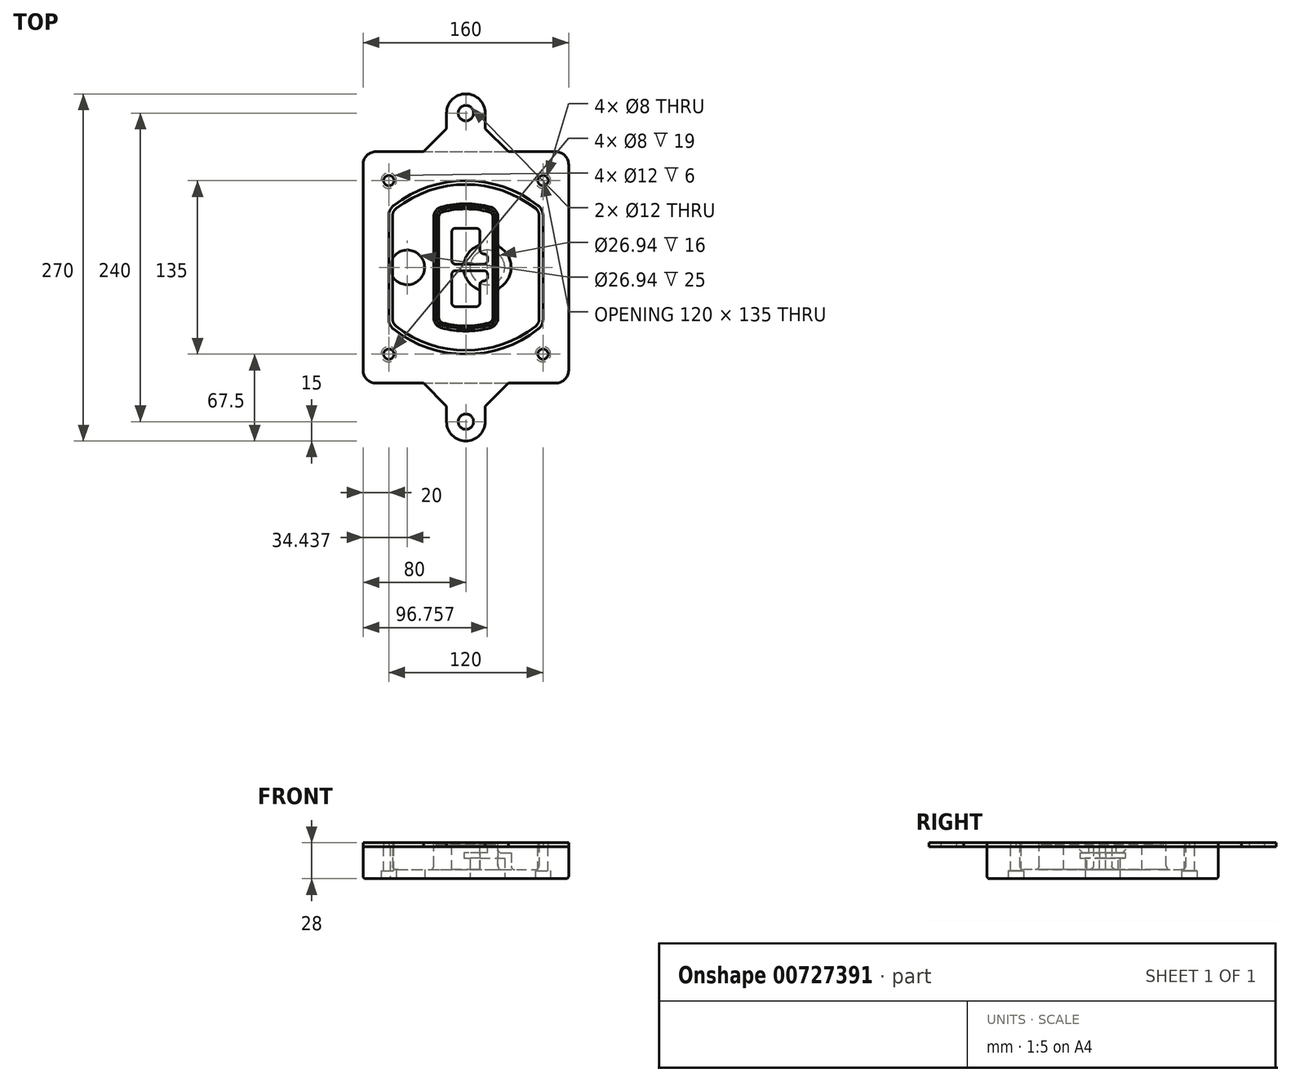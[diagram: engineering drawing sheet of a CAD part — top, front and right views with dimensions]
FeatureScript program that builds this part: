
annotation { "Feature Type Name" : "Feature", "Feature Type Description" : "" }
export const myFeature = defineFeature(function(context is Context, id is Id, definition is map)
    precondition{}
    {
        {
            var Q0;
            Q0=qCreatedBy(makeId("Top.planeOp"),FACE);
            var sketch = newSketch(context, id + "F0", { "sketchPlane" : qUnion([Q0])});
            skPoint(sketch, "E0.rect.middle", {"position": v(0, 0) * mm});
            skLineSegment(sketch, "E1.bottom", {"start": v(-70, -90) * mm, "end": v(70, -90) * mm});
            skLineSegment(sketch, "E1.top", {"start": v(-70, 90) * mm, "end": v(70, 90) * mm});
            skLineSegment(sketch, "E1.left", {"start": v(-80, -80) * mm, "end": v(-80, 80) * mm});
            skLineSegment(sketch, "E1.right", {"start": v(80, -80) * mm, "end": v(80, 80) * mm});
            skLineSegment(sketch, "E2", {"start": v(-80, 90) * mm, "end": v(80, -90) * mm, "construction": true});
            skLineSegment(sketch, "E3", {"start": v(80, 90) * mm, "end": v(-80, -90) * mm, "construction": true});
            skCircle(sketch, "E4", {"center": v(-60, 67.5) * mm, "radius": 4 * mm});
            skCircle(sketch, "E5", {"center": v(60, 67.5) * mm, "radius": 4 * mm});
            skCircle(sketch, "E6", {"center": v(60, -67.5) * mm, "radius": 4 * mm});
            skCircle(sketch, "E7", {"center": v(-60, -67.5) * mm, "radius": 4 * mm});
            skLineSegment(sketch, "E8", {"start": v(-60, 67.5) * mm, "end": v(60, 67.5) * mm, "construction": true});
            skLineSegment(sketch, "E9", {"start": v(60, 67.5) * mm, "end": v(60, -67.5) * mm, "construction": true});
            skLineSegment(sketch, "E10", {"start": v(60, -67.5) * mm, "end": v(-60, -67.5) * mm, "construction": true});
            skLineSegment(sketch, "E11", {"start": v(-60, -67.5) * mm, "end": v(-60, 67.5) * mm, "construction": true});
            skLineSegment(sketch, "E12", {"start": v(-60, 40.3) * mm, "end": v(-60, -40.3) * mm});
            skLineSegment(sketch, "E13", {"start": v(60, 40.3) * mm, "end": v(60, -40.3) * mm});
            skArc(sketch, "E14", {"start": v(56.15, 48.18) * mm, "mid": v(0, 67.5) * mm, "end": v(-56.15, 48.18) * mm});
            skArc(sketch, "E15", {"start": v(-56.15, -48.18) * mm, "mid": v(0, -67.5) * mm, "end": v(56.15, -48.18) * mm});
            skLineSegment(sketch, "E16", {"start": v(-60, 0) * mm, "end": v(60, 0) * mm, "construction": true});
            skPoint(sketch, "E17.visualSharp", {"position": v(-60, -45) * mm});
            skArc(sketch, "E17.filletArc", {"start": v(-60, -40.3) * mm, "mid": v(-58.99, -44.68) * mm, "end": v(-56.15, -48.18) * mm});
            skPoint(sketch, "E18.visualSharp", {"position": v(-60, 45) * mm});
            skArc(sketch, "E18.filletArc", {"start": v(-56.15, 48.18) * mm, "mid": v(-58.99, 44.68) * mm, "end": v(-60, 40.3) * mm});
            skPoint(sketch, "E19.visualSharp", {"position": v(60, 45) * mm});
            skArc(sketch, "E19.filletArc", {"start": v(60, 40.3) * mm, "mid": v(58.99, 44.68) * mm, "end": v(56.15, 48.18) * mm});
            skPoint(sketch, "E20.visualSharp", {"position": v(60, -45) * mm});
            skArc(sketch, "E20.filletArc", {"start": v(56.15, -48.18) * mm, "mid": v(58.99, -44.68) * mm, "end": v(60, -40.3) * mm});
            skPoint(sketch, "E21.visualSharp", {"position": v(-80, 90) * mm});
            skArc(sketch, "E21.filletArc", {"start": v(-70, 90) * mm, "mid": v(-77.07, 87.07) * mm, "end": v(-80, 80) * mm});
            skPoint(sketch, "E22.visualSharp", {"position": v(80, 90) * mm});
            skArc(sketch, "E22.filletArc", {"start": v(80, 80) * mm, "mid": v(77.07, 87.07) * mm, "end": v(70, 90) * mm});
            skPoint(sketch, "E23.visualSharp", {"position": v(80, -90) * mm});
            skArc(sketch, "E23.filletArc", {"start": v(70, -90) * mm, "mid": v(77.07, -87.07) * mm, "end": v(80, -80) * mm});
            skPoint(sketch, "E24.visualSharp", {"position": v(-80, -90) * mm});
            skArc(sketch, "E24.filletArc", {"start": v(-80, -80) * mm, "mid": v(-77.07, -87.07) * mm, "end": v(-70, -90) * mm});
            skArc(sketch, "E25.0", {"start": v(57, 40.3) * mm, "mid": v(56.3, 43.36) * mm, "end": v(54.3, 45.81) * mm});
            skLineSegment(sketch, "E25.1", {"start": v(57, 40.3) * mm, "end": v(57, -40.3) * mm});
            skArc(sketch, "E25.2", {"start": v(54.3, -45.81) * mm, "mid": v(56.3, -43.36) * mm, "end": v(57, -40.3) * mm});
            skArc(sketch, "E25.3", {"start": v(-54.3, -45.81) * mm, "mid": v(0, -64.5) * mm, "end": v(54.3, -45.81) * mm});
            skArc(sketch, "E25.4", {"start": v(-57, -40.3) * mm, "mid": v(-56.3, -43.36) * mm, "end": v(-54.3, -45.81) * mm});
            skArc(sketch, "E25.5", {"start": v(54.3, 45.81) * mm, "mid": v(0, 64.5) * mm, "end": v(-54.3, 45.81) * mm});
            skLineSegment(sketch, "E25.6", {"start": v(-57, 40.3) * mm, "end": v(-57, -40.3) * mm});
            skArc(sketch, "E25.7", {"start": v(-54.3, 45.81) * mm, "mid": v(-56.3, 43.36) * mm, "end": v(-57, 40.3) * mm});
            skArc(sketch, "E26.0", {"start": v(-58.62, 51.33) * mm, "mid": v(-62.58, 46.43) * mm, "end": v(-64, 40.3) * mm});
            skArc(sketch, "E26.1", {"start": v(58.62, 51.33) * mm, "mid": v(0, 71.5) * mm, "end": v(-58.62, 51.33) * mm});
            skArc(sketch, "E26.2", {"start": v(64, 40.3) * mm, "mid": v(62.58, 46.43) * mm, "end": v(58.62, 51.33) * mm});
            skLineSegment(sketch, "E26.3", {"start": v(64, 40.3) * mm, "end": v(64, -40.3) * mm});
            skArc(sketch, "E26.4", {"start": v(58.62, -51.33) * mm, "mid": v(62.58, -46.43) * mm, "end": v(64, -40.3) * mm});
            skLineSegment(sketch, "E26.5", {"start": v(-64, 40.3) * mm, "end": v(-64, -40.3) * mm});
            skArc(sketch, "E26.6", {"start": v(-58.62, -51.33) * mm, "mid": v(0, -71.5) * mm, "end": v(58.62, -51.33) * mm});
            skArc(sketch, "E26.7", {"start": v(-64, -40.3) * mm, "mid": v(-62.58, -46.43) * mm, "end": v(-58.62, -51.33) * mm});
            skSolve(sketch);
        }
        {
            var Q0;
            Q0=makeQuery(id+"F0.imprint","IMPRINT",FACE,{"disambiguationData":[TD([[makeQuery(id+"F0.imprint","IMPRINT",EDGE,{"derivedFrom":sQuery(id+"F0.wireOp",EDGE,"E1.bottom")}),1.0]])]});
            var Q1;
            Q1=makeQuery(id+"F0.imprint","IMPRINT",FACE,{"disambiguationData":[TD([[makeQuery(id+"F0.imprint","IMPRINT",EDGE,{"derivedFrom":sQuery(id+"F0.wireOp",EDGE,"E12")}),1.0]])]});
            var Q2;
            Q2=makeQuery(id+"F0.imprint","IMPRINT",FACE,{"disambiguationData":[TD([[makeQuery(id+"F0.imprint","IMPRINT",EDGE,{"derivedFrom":sQuery(id+"F0.wireOp",EDGE,"E25.0")}),1.0]])]});
            var Q3;
            Q3=makeQuery(id+"F0.imprint","IMPRINT",FACE,{"disambiguationData":[TD([[makeQuery(id+"F0.imprint","IMPRINT",EDGE,{"derivedFrom":sQuery(id+"F0.wireOp",EDGE,"E12")}),-1.0]])]});
            extrude(context, id + "F1", {"entities" : qUnion([Q0, Q1, Q2, Q3]), "oppositeDirection" : true, "depth" : 25 * mm});
        }
        {
            var Q0;
            Q0=makeQuery(id+"F0.imprint","IMPRINT",FACE,{"disambiguationData":[TD([[makeQuery(id+"F0.imprint","IMPRINT",EDGE,{"derivedFrom":sQuery(id+"F0.wireOp",EDGE,"E12")}),1.0]])]});
            extrude(context, id + "F2", {"entities" : qUnion([Q0]), "operationType" : NewBodyOperationType.ADD, "depth" : 3 * mm});
        }
        {
            var Q0;
            Q0=makeQuery(id+"F0.imprint","IMPRINT",FACE,{"disambiguationData":[TD([[makeQuery(id+"F0.imprint","IMPRINT",EDGE,{"derivedFrom":sQuery(id+"F0.wireOp",EDGE,"E25.0")}),1.0]])]});
            extrude(context, id + "F3", {"entities" : qUnion([Q0]), "operationType" : NewBodyOperationType.REMOVE, "oppositeDirection" : true, "depth" : 18 * mm});
        }
        {
            var Q0;
            Q0=makeQuery(id+"F2.opExtrude","CAP_FACE",FACE,{"disambiguationData":[OSD([sQuery(id+"F0.wireOp",EDGE,"E12"),sQuery(id+"F0.wireOp",EDGE,"E13"),sQuery(id+"F0.wireOp",EDGE,"E14"),sQuery(id+"F0.wireOp",EDGE,"E15"),sQuery(id+"F0.wireOp",EDGE,"E17.filletArc"),sQuery(id+"F0.wireOp",EDGE,"E18.filletArc"),sQuery(id+"F0.wireOp",EDGE,"E19.filletArc"),sQuery(id+"F0.wireOp",EDGE,"E20.filletArc"),sQuery(id+"F0.wireOp",EDGE,"E25.0"),sQuery(id+"F0.wireOp",EDGE,"E25.1"),sQuery(id+"F0.wireOp",EDGE,"E25.2"),sQuery(id+"F0.wireOp",EDGE,"E25.3"),sQuery(id+"F0.wireOp",EDGE,"E25.4"),sQuery(id+"F0.wireOp",EDGE,"E25.5"),sQuery(id+"F0.wireOp",EDGE,"E25.6"),sQuery(id+"F0.wireOp",EDGE,"E25.7")])],"isStart":false});
            var sketch = newSketch(context, id + "F4", { "sketchPlane" : qUnion([Q0])});
            skArc(sketch, "E27.0", {"start": v(-19.08, -46.97) * mm, "mid": v(0, -49.5) * mm, "end": v(19.08, -46.97) * mm});
            skArc(sketch, "E28.0", {"start": v(19.08, 46.97) * mm, "mid": v(0, 49.5) * mm, "end": v(-19.08, 46.97) * mm});
            skLineSegment(sketch, "E29", {"start": v(-25, 39.25) * mm, "end": v(-25, -39.25) * mm});
            skLineSegment(sketch, "E30", {"start": v(25, 39.25) * mm, "end": v(25, -39.25) * mm});
            skLineSegment(sketch, "E31", {"start": v(-25, 45.1) * mm, "end": v(25, 45.1) * mm, "construction": true});
            skLineSegment(sketch, "E32", {"start": v(-25, -45.1) * mm, "end": v(25, -45.1) * mm, "construction": true});
            skPoint(sketch, "E33.visualSharp", {"position": v(-25, 45.1) * mm});
            skArc(sketch, "E33.filletArc", {"start": v(-19.08, 46.97) * mm, "mid": v(-23.35, 44.11) * mm, "end": v(-25, 39.25) * mm});
            skPoint(sketch, "E34.visualSharp", {"position": v(25, 45.1) * mm});
            skArc(sketch, "E34.filletArc", {"start": v(25, 39.25) * mm, "mid": v(23.35, 44.11) * mm, "end": v(19.08, 46.97) * mm});
            skPoint(sketch, "E35.visualSharp", {"position": v(25, -45.1) * mm});
            skArc(sketch, "E35.filletArc", {"start": v(19.08, -46.97) * mm, "mid": v(23.35, -44.11) * mm, "end": v(25, -39.25) * mm});
            skPoint(sketch, "E36.visualSharp", {"position": v(-25, -45.1) * mm});
            skArc(sketch, "E36.filletArc", {"start": v(-25, -39.25) * mm, "mid": v(-23.35, -44.11) * mm, "end": v(-19.08, -46.97) * mm});
            skArc(sketch, "E37.0", {"start": v(54.3, 45.81) * mm, "mid": v(0, 64.5) * mm, "end": v(-54.3, 45.81) * mm});
            skArc(sketch, "E37.1", {"start": v(-54.3, 45.81) * mm, "mid": v(-56.3, 43.36) * mm, "end": v(-57, 40.3) * mm});
            skLineSegment(sketch, "E37.2", {"start": v(-57, 40.3) * mm, "end": v(-57, -40.3) * mm});
            skArc(sketch, "E37.3", {"start": v(-57, -40.3) * mm, "mid": v(-56.3, -43.36) * mm, "end": v(-54.3, -45.81) * mm});
            skArc(sketch, "E37.4", {"start": v(-54.3, -45.81) * mm, "mid": v(0, -64.5) * mm, "end": v(54.3, -45.81) * mm});
            skArc(sketch, "E37.5", {"start": v(54.3, -45.81) * mm, "mid": v(56.3, -43.36) * mm, "end": v(57, -40.3) * mm});
            skLineSegment(sketch, "E37.6", {"start": v(57, 40.3) * mm, "end": v(57, -40.3) * mm});
            skArc(sketch, "E37.7", {"start": v(57, 40.3) * mm, "mid": v(56.3, 43.36) * mm, "end": v(54.3, 45.81) * mm});
            skLineSegment(sketch, "E38.0", {"start": v(23, 39.25) * mm, "end": v(23, -39.25) * mm});
            skArc(sketch, "E38.1", {"start": v(18.56, -45.04) * mm, "mid": v(21.76, -42.9) * mm, "end": v(23, -39.25) * mm});
            skArc(sketch, "E38.2", {"start": v(-18.56, -45.04) * mm, "mid": v(0, -47.5) * mm, "end": v(18.56, -45.04) * mm});
            skArc(sketch, "E38.3", {"start": v(-23, -39.25) * mm, "mid": v(-21.76, -42.9) * mm, "end": v(-18.56, -45.04) * mm});
            skLineSegment(sketch, "E38.4", {"start": v(-23, 39.25) * mm, "end": v(-23, -39.25) * mm});
            skArc(sketch, "E38.5", {"start": v(23, 39.25) * mm, "mid": v(21.76, 42.9) * mm, "end": v(18.56, 45.04) * mm});
            skArc(sketch, "E38.6", {"start": v(-18.56, 45.04) * mm, "mid": v(-21.76, 42.9) * mm, "end": v(-23, 39.25) * mm});
            skArc(sketch, "E38.7", {"start": v(18.56, 45.04) * mm, "mid": v(0, 47.5) * mm, "end": v(-18.56, 45.04) * mm});
            skArc(sketch, "E39.0", {"start": v(21, 39.25) * mm, "mid": v(20.18, 41.68) * mm, "end": v(18.04, 43.1) * mm});
            skLineSegment(sketch, "E39.1", {"start": v(21, 39.25) * mm, "end": v(21, -39.25) * mm});
            skArc(sketch, "E39.2", {"start": v(18.04, -43.1) * mm, "mid": v(20.18, -41.68) * mm, "end": v(21, -39.25) * mm});
            skArc(sketch, "E39.3", {"start": v(-18.04, -43.1) * mm, "mid": v(0, -45.5) * mm, "end": v(18.04, -43.1) * mm});
            skArc(sketch, "E39.4", {"start": v(-21, -39.25) * mm, "mid": v(-20.18, -41.68) * mm, "end": v(-18.04, -43.1) * mm});
            skArc(sketch, "E39.5", {"start": v(18.04, 43.1) * mm, "mid": v(0, 45.5) * mm, "end": v(-18.04, 43.1) * mm});
            skLineSegment(sketch, "E39.6", {"start": v(-21, 39.25) * mm, "end": v(-21, -39.25) * mm});
            skArc(sketch, "E39.7", {"start": v(-18.04, 43.1) * mm, "mid": v(-20.18, 41.68) * mm, "end": v(-21, 39.25) * mm});
            skLineSegment(sketch, "E40", {"start": v(-25, 0) * mm, "end": v(25, 0) * mm, "construction": true});
            skLineSegment(sketch, "E41", {"start": v(-11, 5.5) * mm, "end": v(-11, 27.5) * mm});
            skLineSegment(sketch, "E42", {"start": v(-8, 30.5) * mm, "end": v(8, 30.5) * mm});
            skLineSegment(sketch, "E43", {"start": v(11, 27.5) * mm, "end": v(11, 13.5) * mm});
            skLineSegment(sketch, "E44", {"start": v(14, 10.5) * mm, "end": v(14, 10.5) * mm});
            skLineSegment(sketch, "E45", {"start": v(17, 7.5) * mm, "end": v(17, 5.5) * mm});
            skLineSegment(sketch, "E46", {"start": v(14, 2.5) * mm, "end": v(-8, 2.5) * mm});
            skPoint(sketch, "E47.visualSharp", {"position": v(-11, 30.5) * mm});
            skArc(sketch, "E47.filletArc", {"start": v(-8, 30.5) * mm, "mid": v(-10.12, 29.62) * mm, "end": v(-11, 27.5) * mm});
            skPoint(sketch, "E48.visualSharp", {"position": v(11, 30.5) * mm});
            skArc(sketch, "E48.filletArc", {"start": v(11, 27.5) * mm, "mid": v(10.12, 29.62) * mm, "end": v(8, 30.5) * mm});
            skPoint(sketch, "E49.visualSharp", {"position": v(11, 10.5) * mm});
            skArc(sketch, "E49.filletArc", {"start": v(11, 13.5) * mm, "mid": v(11.88, 11.38) * mm, "end": v(14, 10.5) * mm});
            skPoint(sketch, "E50.visualSharp", {"position": v(17, 10.5) * mm});
            skArc(sketch, "E50.filletArc", {"start": v(17, 7.5) * mm, "mid": v(16.12, 9.62) * mm, "end": v(14, 10.5) * mm});
            skPoint(sketch, "E51.visualSharp", {"position": v(17, 2.5) * mm});
            skArc(sketch, "E51.filletArc", {"start": v(14, 2.5) * mm, "mid": v(16.12, 3.38) * mm, "end": v(17, 5.5) * mm});
            skPoint(sketch, "E52.visualSharp", {"position": v(-11, 2.5) * mm});
            skArc(sketch, "E52.filletArc", {"start": v(-11, 5.5) * mm, "mid": v(-10.12, 3.38) * mm, "end": v(-8, 2.5) * mm});
            skLineSegment(sketch, "E53.0.MirrorCS", {"start": v(14, -2.5) * mm, "end": v(-8, -2.5) * mm});
            skArc(sketch, "E54.0.MirrorCS", {"start": v(-11, -5.5) * mm, "mid": v(-10.12, -3.38) * mm, "end": v(-8, -2.5) * mm});
            skLineSegment(sketch, "E55.0.MirrorCS", {"start": v(-11, -5.5) * mm, "end": v(-11, -27.5) * mm});
            skArc(sketch, "E56.0.MirrorCS", {"start": v(-8, -30.5) * mm, "mid": v(-10.12, -29.62) * mm, "end": v(-11, -27.5) * mm});
            skLineSegment(sketch, "E57.0.MirrorCS", {"start": v(-8, -30.5) * mm, "end": v(8, -30.5) * mm});
            skArc(sketch, "E58.0.MirrorCS", {"start": v(11, -27.5) * mm, "mid": v(10.12, -29.62) * mm, "end": v(8, -30.5) * mm});
            skLineSegment(sketch, "E59.0.MirrorCS", {"start": v(11, -27.5) * mm, "end": v(11, -13.5) * mm});
            skArc(sketch, "E60.0.MirrorCS", {"start": v(11, -13.5) * mm, "mid": v(11.88, -11.38) * mm, "end": v(14, -10.5) * mm});
            skArc(sketch, "E61.0.MirrorCS", {"start": v(17, -7.5) * mm, "mid": v(16.12, -9.62) * mm, "end": v(14, -10.5) * mm});
            skLineSegment(sketch, "E62.0.MirrorCS", {"start": v(17, -7.5) * mm, "end": v(17, -5.5) * mm});
            skArc(sketch, "E63.0.MirrorCS", {"start": v(14, -2.5) * mm, "mid": v(16.12, -3.38) * mm, "end": v(17, -5.5) * mm});
            skSolve(sketch);
        }
        {
            var Q0;
            Q0=makeQuery(id+"F4.imprint","IMPRINT",FACE,{"disambiguationData":[TD([[makeQuery(id+"F4.imprint","IMPRINT",EDGE,{"derivedFrom":sQuery(id+"F4.wireOp",EDGE,"E27.0")}),1.0]])]});
            var Q1;
            Q1=makeQuery(id+"F4.imprint","IMPRINT",FACE,{"disambiguationData":[TD([[makeQuery(id+"F4.imprint","IMPRINT",EDGE,{"derivedFrom":sQuery(id+"F4.wireOp",EDGE,"E38.0")}),-1.0]])]});
            var Q2;
            Q2=makeQuery(id+"F4.imprint","IMPRINT",FACE,{"disambiguationData":[TD([[makeQuery(id+"F4.imprint","IMPRINT",EDGE,{"derivedFrom":sQuery(id+"F4.wireOp",EDGE,"E39.0")}),1.0]])]});
            extrude(context, id + "F5", {"entities" : qUnion([Q0, Q1, Q2]), "operationType" : NewBodyOperationType.ADD, "endBound" : BoundingType.UP_TO_NEXT, "oppositeDirection" : true, "depth" : 25 * mm});
        }
        {
            var Q0;
            Q0=makeQuery(id+"F4.imprint","IMPRINT",FACE,{"disambiguationData":[TD([[makeQuery(id+"F4.imprint","IMPRINT",EDGE,{"derivedFrom":sQuery(id+"F4.wireOp",EDGE,"E38.0")}),-1.0]])]});
            extrude(context, id + "F6", {"entities" : qUnion([Q0]), "operationType" : NewBodyOperationType.REMOVE, "oppositeDirection" : true, "depth" : 2 * mm});
        }
        {
            var Q0;
            Q0=makeQuery(id+"F1.opExtrude","CAP_FACE",FACE,{"disambiguationData":[OSD([sQuery(id+"F0.wireOp",EDGE,"E1.bottom"),sQuery(id+"F0.wireOp",EDGE,"E1.top"),sQuery(id+"F0.wireOp",EDGE,"E1.left"),sQuery(id+"F0.wireOp",EDGE,"E1.right"),sQuery(id+"F0.wireOp",EDGE,"E4"),sQuery(id+"F0.wireOp",EDGE,"E5"),sQuery(id+"F0.wireOp",EDGE,"E6"),sQuery(id+"F0.wireOp",EDGE,"E7"),sQuery(id+"F0.wireOp",EDGE,"E21.filletArc"),sQuery(id+"F0.wireOp",EDGE,"E22.filletArc"),sQuery(id+"F0.wireOp",EDGE,"E23.filletArc"),sQuery(id+"F0.wireOp",EDGE,"E24.filletArc")])],"isStart":false});
            var sketch = newSketch(context, id + "F7", { "sketchPlane" : qUnion([Q0])});
            skCircle(sketch, "E64", {"center": v(16.76, 0) * mm, "radius": 13.47 * mm});
            skCircle(sketch, "E65", {"center": v(-45.56, 0) * mm, "radius": 13.47 * mm});
            skLineSegment(sketch, "E66", {"start": v(80, 0) * mm, "end": v(-80, 0) * mm});
            skCircle(sketch, "E67", {"center": v(16.76, 0) * mm, "radius": 18.47 * mm});
            skCircle(sketch, "E68", {"center": v(60, -67.5) * mm, "radius": 6 * mm});
            skCircle(sketch, "E69", {"center": v(-60, -67.5) * mm, "radius": 6 * mm});
            skCircle(sketch, "E70", {"center": v(-60, 67.5) * mm, "radius": 6 * mm});
            skCircle(sketch, "E71", {"center": v(60, 67.5) * mm, "radius": 6 * mm});
            skSolve(sketch);
        }
        {
            var Q0;
            {var subQ1=sQuery(id+"F7.wireOp",EDGE,"E66");var subQ4=sQuery(id+"F7.wireOp",EDGE,"E64");var subQ6=makeQuery(id+"F7.imprint","INTERSECT",VERTEX,{"disambiguationData":[OD(0.0)],"derivedFrom":[subQ4,subQ1]});Q0=makeQuery(id+"F7.imprint","IMPRINT",FACE,{"disambiguationData":[TD([[makeQuery(id+"F7.imprint","IMPRINT",EDGE,{"disambiguationData":[TD([[subQ6,-1.0]])],"derivedFrom":subQ4}),-1.0]])]});}
            var Q1;
            {var subQ0=sQuery(id+"F7.wireOp",EDGE,"E66");var subQ1=sQuery(id+"F7.wireOp",EDGE,"E64");var subQ3=makeQuery(id+"F7.imprint","INTERSECT",VERTEX,{"disambiguationData":[OD(0.0)],"derivedFrom":[subQ1,subQ0]});Q1=makeQuery(id+"F7.imprint","IMPRINT",FACE,{"disambiguationData":[TD([[makeQuery(id+"F7.imprint","IMPRINT",EDGE,{"disambiguationData":[TD([[subQ3,-1.0]])],"derivedFrom":subQ1}),1.0]])]});}
            var Q2;
            {var subQ0=sQuery(id+"F7.wireOp",EDGE,"E66");var subQ1=sQuery(id+"F7.wireOp",EDGE,"E64");var subQ3=makeQuery(id+"F7.imprint","INTERSECT",VERTEX,{"disambiguationData":[OD(0.0)],"derivedFrom":[subQ1,subQ0]});Q2=makeQuery(id+"F7.imprint","IMPRINT",FACE,{"disambiguationData":[TD([[makeQuery(id+"F7.imprint","IMPRINT",EDGE,{"disambiguationData":[TD([[subQ3,1.0]])],"derivedFrom":subQ1}),1.0]])]});}
            var Q3;
            {var subQ1=sQuery(id+"F7.wireOp",EDGE,"E66");var subQ4=sQuery(id+"F7.wireOp",EDGE,"E64");var subQ6=makeQuery(id+"F7.imprint","INTERSECT",VERTEX,{"disambiguationData":[OD(0.0)],"derivedFrom":[subQ4,subQ1]});Q3=makeQuery(id+"F7.imprint","IMPRINT",FACE,{"disambiguationData":[TD([[makeQuery(id+"F7.imprint","IMPRINT",EDGE,{"disambiguationData":[TD([[subQ6,1.0]])],"derivedFrom":subQ4}),-1.0]])]});}
            extrude(context, id + "F8", {"entities" : qUnion([Q0, Q1, Q2, Q3]), "operationType" : NewBodyOperationType.ADD, "oppositeDirection" : true, "depth" : 20 * mm});
        }
        {
            var Q0;
            {var subQ0=sQuery(id+"F7.wireOp",EDGE,"E66");var subQ1=sQuery(id+"F7.wireOp",EDGE,"E64");var subQ3=makeQuery(id+"F7.imprint","INTERSECT",VERTEX,{"disambiguationData":[OD(0.0)],"derivedFrom":[subQ1,subQ0]});Q0=makeQuery(id+"F7.imprint","IMPRINT",FACE,{"disambiguationData":[TD([[makeQuery(id+"F7.imprint","IMPRINT",EDGE,{"disambiguationData":[TD([[subQ3,-1.0]])],"derivedFrom":subQ1}),1.0]])]});}
            var Q1;
            {var subQ0=sQuery(id+"F7.wireOp",EDGE,"E66");var subQ1=sQuery(id+"F7.wireOp",EDGE,"E64");var subQ3=makeQuery(id+"F7.imprint","INTERSECT",VERTEX,{"disambiguationData":[OD(0.0)],"derivedFrom":[subQ1,subQ0]});Q1=makeQuery(id+"F7.imprint","IMPRINT",FACE,{"disambiguationData":[TD([[makeQuery(id+"F7.imprint","IMPRINT",EDGE,{"disambiguationData":[TD([[subQ3,1.0]])],"derivedFrom":subQ1}),1.0]])]});}
            extrude(context, id + "F9", {"entities" : qUnion([Q0, Q1]), "operationType" : NewBodyOperationType.REMOVE, "oppositeDirection" : true, "depth" : 16 * mm});
        }
        {
            var Q0;
            {var subQ0=sQuery(id+"F7.wireOp",EDGE,"E66");var subQ1=sQuery(id+"F7.wireOp",EDGE,"E65");var subQ3=makeQuery(id+"F7.imprint","INTERSECT",VERTEX,{"disambiguationData":[OD(0.0)],"derivedFrom":[subQ1,subQ0]});Q0=makeQuery(id+"F7.imprint","IMPRINT",FACE,{"disambiguationData":[TD([[makeQuery(id+"F7.imprint","IMPRINT",EDGE,{"disambiguationData":[TD([[subQ3,-1.0]])],"derivedFrom":subQ1}),1.0]])]});}
            var Q1;
            {var subQ0=sQuery(id+"F7.wireOp",EDGE,"E66");var subQ1=sQuery(id+"F7.wireOp",EDGE,"E65");var subQ3=makeQuery(id+"F7.imprint","INTERSECT",VERTEX,{"disambiguationData":[OD(0.0)],"derivedFrom":[subQ1,subQ0]});Q1=makeQuery(id+"F7.imprint","IMPRINT",FACE,{"disambiguationData":[TD([[makeQuery(id+"F7.imprint","IMPRINT",EDGE,{"disambiguationData":[TD([[subQ3,1.0]])],"derivedFrom":subQ1}),1.0]])]});}
            extrude(context, id + "F10", {"entities" : qUnion([Q0, Q1]), "operationType" : NewBodyOperationType.REMOVE, "oppositeDirection" : true, "depth" : 25 * mm});
        }
        {
            var Q0;
            Q0=makeQuery(id+"F7.imprint","IMPRINT",FACE,{"disambiguationData":[TD([[makeQuery(id+"F7.imprint","IMPRINT",EDGE,{"derivedFrom":sQuery(id+"F7.wireOp",EDGE,"E68")}),1.0]])]});
            var Q1;
            Q1=makeQuery(id+"F7.imprint","IMPRINT",FACE,{"disambiguationData":[TD([[makeQuery(id+"F7.imprint","IMPRINT",EDGE,{"derivedFrom":makeQuery(id+"F1.opExtrude","CAP_EDGE",EDGE,{"disambiguationData":[OSD([sQuery(id+"F0.wireOp",EDGE,"E5")])],"isStart":false})}),-1.0]])]});
            var Q2;
            Q2=makeQuery(id+"F7.imprint","IMPRINT",FACE,{"disambiguationData":[TD([[makeQuery(id+"F7.imprint","IMPRINT",EDGE,{"derivedFrom":sQuery(id+"F7.wireOp",EDGE,"E69")}),1.0]])]});
            var Q3;
            Q3=makeQuery(id+"F7.imprint","IMPRINT",FACE,{"disambiguationData":[TD([[makeQuery(id+"F7.imprint","IMPRINT",EDGE,{"derivedFrom":makeQuery(id+"F1.opExtrude","CAP_EDGE",EDGE,{"disambiguationData":[OSD([sQuery(id+"F0.wireOp",EDGE,"E4")])],"isStart":false})}),-1.0]])]});
            var Q4;
            Q4=makeQuery(id+"F7.imprint","IMPRINT",FACE,{"disambiguationData":[TD([[makeQuery(id+"F7.imprint","IMPRINT",EDGE,{"derivedFrom":sQuery(id+"F7.wireOp",EDGE,"E70")}),1.0]])]});
            var Q5;
            Q5=makeQuery(id+"F7.imprint","IMPRINT",FACE,{"disambiguationData":[TD([[makeQuery(id+"F7.imprint","IMPRINT",EDGE,{"derivedFrom":makeQuery(id+"F1.opExtrude","CAP_EDGE",EDGE,{"disambiguationData":[OSD([sQuery(id+"F0.wireOp",EDGE,"E7")])],"isStart":false})}),-1.0]])]});
            var Q6;
            Q6=makeQuery(id+"F7.imprint","IMPRINT",FACE,{"disambiguationData":[TD([[makeQuery(id+"F7.imprint","IMPRINT",EDGE,{"derivedFrom":sQuery(id+"F7.wireOp",EDGE,"E71")}),1.0]])]});
            var Q7;
            Q7=makeQuery(id+"F7.imprint","IMPRINT",FACE,{"disambiguationData":[TD([[makeQuery(id+"F7.imprint","IMPRINT",EDGE,{"derivedFrom":makeQuery(id+"F1.opExtrude","CAP_EDGE",EDGE,{"disambiguationData":[OSD([sQuery(id+"F0.wireOp",EDGE,"E6")])],"isStart":false})}),-1.0]])]});
            extrude(context, id + "F11", {"entities" : qUnion([Q0, Q1, Q2, Q3, Q4, Q5, Q6, Q7]), "operationType" : NewBodyOperationType.REMOVE, "oppositeDirection" : true, "depth" : 6 * mm});
        }
        {
            var Q0;
            Q0=makeQuery(id+"F9.boolean.opBoolean","COPY",FACE,{"derivedFrom":makeQuery(id+"F9.opExtrude","CAP_FACE",FACE,{"disambiguationData":[OSD([sQuery(id+"F7.wireOp",EDGE,"E64")])],"isStart":false})});
            var sketch = newSketch(context, id + "F12", { "sketchPlane" : qUnion([Q0])});
            skArc(sketch, "E72.0", {"start": v(11, 17.55) * mm, "mid": v(2.57, 11.82) * mm, "end": v(-1.54, 2.5) * mm});
            skArc(sketch, "E72.1", {"start": v(-1.54, -2.5) * mm, "mid": v(2.57, -11.82) * mm, "end": v(11, -17.55) * mm});
            skLineSegment(sketch, "E73", {"start": v(-1.54, -2.5) * mm, "end": v(14, -2.5) * mm});
            skLineSegment(sketch, "E74.0", {"start": v(14, 2.5) * mm, "end": v(-1.54, 2.5) * mm});
            skArc(sketch, "E74.1", {"start": v(14, 2.5) * mm, "mid": v(16.12, 3.38) * mm, "end": v(17, 5.5) * mm});
            skLineSegment(sketch, "E74.2", {"start": v(17, 7.5) * mm, "end": v(17, 5.5) * mm});
            skArc(sketch, "E74.3", {"start": v(17, 7.5) * mm, "mid": v(16.12, 9.62) * mm, "end": v(14, 10.5) * mm});
            skArc(sketch, "E74.4", {"start": v(11, 13.5) * mm, "mid": v(11.88, 11.38) * mm, "end": v(14, 10.5) * mm});
            skLineSegment(sketch, "E74.5", {"start": v(11, 17.55) * mm, "end": v(11, 13.5) * mm});
            skLineSegment(sketch, "E74.7", {"start": v(14, -2.5) * mm, "end": v(-1.54, -2.5) * mm});
            skArc(sketch, "E74.8", {"start": v(14, -2.5) * mm, "mid": v(16.12, -3.38) * mm, "end": v(17, -5.5) * mm});
            skLineSegment(sketch, "E74.9", {"start": v(17, -7.5) * mm, "end": v(17, -5.5) * mm});
            skArc(sketch, "E74.10", {"start": v(17, -7.5) * mm, "mid": v(16.12, -9.62) * mm, "end": v(14, -10.5) * mm});
            skArc(sketch, "E74.11", {"start": v(11, -13.5) * mm, "mid": v(11.88, -11.38) * mm, "end": v(14, -10.5) * mm});
            skLineSegment(sketch, "E74.12", {"start": v(11, -17.55) * mm, "end": v(11, -13.5) * mm});
            skPoint(sketch, "E75.orphan", {"position": v(11, -27.5) * mm});
            skPoint(sketch, "E76.orphan", {"position": v(-8, -2.5) * mm});
            skPoint(sketch, "E77.orphan", {"position": v(-8, 2.5) * mm});
            skPoint(sketch, "E78.orphan", {"position": v(11, 27.5) * mm});
            skSolve(sketch);
        }
        {
            var Q0;
            {var subQ7=sQuery(id+"F12.wireOp",EDGE,"E72.0");var subQ14=sQuery(id+"F12.wireOp",EDGE,"E72.1");var subQ16=sQuery(id+"F12.wireOp",EDGE,"E74.1");var subQ18=sQuery(id+"F12.wireOp",EDGE,"E74.8");Q0=qUnion([makeQuery(id+"F12.imprint","IMPRINT",FACE,{"disambiguationData":[TD([[makeQuery(id+"F12.imprint","IMPRINT",EDGE,{"derivedFrom":subQ7}),1.0]])]}),makeQuery(id+"F12.imprint","IMPRINT",FACE,{"disambiguationData":[TD([[makeQuery(id+"F12.imprint","IMPRINT",EDGE,{"derivedFrom":subQ14}),1.0]])]}),makeQuery(id+"F12.imprint","IMPRINT",FACE,{"disambiguationData":[TD([[makeQuery(id+"F12.imprint","IMPRINT",EDGE,{"derivedFrom":subQ16}),1.0]])]}),makeQuery(id+"F12.imprint","IMPRINT",FACE,{"disambiguationData":[TD([[makeQuery(id+"F12.imprint","IMPRINT",EDGE,{"derivedFrom":subQ18}),-1.0]])]})]);}
            var Q1;
            Q1=makeQuery(id+"F5.boolean.opBoolean","SPLIT",FACE,{"disambiguationData":[TD([makeQuery(id+"F5.opExtrude","SWEPT_FACE",FACE,{"disambiguationData":[OSD([sQuery(id+"F4.wireOp",EDGE,"E41")])]})])],"derivedFrom":makeQuery(id+"F3.boolean.opBoolean","COPY",FACE,{"derivedFrom":makeQuery(id+"F3.opExtrude","CAP_FACE",FACE,{"disambiguationData":[OSD([sQuery(id+"F0.wireOp",EDGE,"E25.0"),sQuery(id+"F0.wireOp",EDGE,"E25.1"),sQuery(id+"F0.wireOp",EDGE,"E25.2"),sQuery(id+"F0.wireOp",EDGE,"E25.3"),sQuery(id+"F0.wireOp",EDGE,"E25.4"),sQuery(id+"F0.wireOp",EDGE,"E25.5"),sQuery(id+"F0.wireOp",EDGE,"E25.6"),sQuery(id+"F0.wireOp",EDGE,"E25.7")])],"isStart":false})})});
            extrude(context, id + "F13", {"entities" : qUnion([Q0]), "operationType" : NewBodyOperationType.REMOVE, "endBound" : BoundingType.UP_TO_SURFACE, "endBoundEntityFace" : qUnion([Q1]), "depth" : 25 * mm});
        }
        {
            var Q0;
            Q0=makeQuery(id+"F3.boolean.opBoolean","COPY",EDGE,{"derivedFrom":makeQuery(id+"F3.opExtrude","CAP_EDGE",EDGE,{"disambiguationData":[OSD([sQuery(id+"F0.wireOp",EDGE,"E25.6")])],"isStart":false})});
            var Q1;
            Q1=makeQuery(id+"F8.boolean.opBoolean","INTERSECT",EDGE,{"derivedFrom":[makeQuery(id+"F5.opExtrude","SWEPT_FACE",FACE,{"disambiguationData":[OSD([sQuery(id+"F4.wireOp",EDGE,"E30")])]}),makeQuery(id+"F8.opExtrude","CAP_FACE",FACE,{"disambiguationData":[OSD([sQuery(id+"F7.wireOp",EDGE,"E67")])],"isStart":false})]});
            var Q2;
            Q2=makeQuery(id+"F8.boolean.opBoolean","INTERSECT",EDGE,{"disambiguationData":[OD(1.0)],"derivedFrom":[makeQuery(id+"F5.opExtrude","SWEPT_FACE",FACE,{"disambiguationData":[OSD([sQuery(id+"F4.wireOp",EDGE,"E30")])]}),makeQuery(id+"F8.opExtrude","SWEPT_FACE",FACE,{"disambiguationData":[OSD([sQuery(id+"F7.wireOp",EDGE,"E67")])]})]});
            var Q3;
            {var subQ0=sQuery(id+"F4.wireOp",EDGE,"E30");Q3=makeQuery(id+"F8.boolean.opBoolean","SPLIT",EDGE,{"disambiguationData":[TD([makeQuery(id+"F5.opExtrude","SWEPT_FACE",FACE,{"disambiguationData":[OSD([sQuery(id+"F4.wireOp",EDGE,"E35.filletArc")])]})])],"derivedFrom":makeQuery(id+"F5.opExtrude","CAP_EDGE",EDGE,{"disambiguationData":[OSD([subQ0])],"isStart":false})});}
            var Q4;
            {var subQ0=sQuery(id+"F0.wireOp",EDGE,"E25.7");var subQ1=sQuery(id+"F0.wireOp",EDGE,"E25.1");var subQ2=sQuery(id+"F0.wireOp",EDGE,"E25.6");var subQ3=sQuery(id+"F0.wireOp",EDGE,"E25.5");var subQ4=sQuery(id+"F0.wireOp",EDGE,"E25.4");var subQ5=sQuery(id+"F0.wireOp",EDGE,"E25.0");var subQ6=sQuery(id+"F0.wireOp",EDGE,"E25.2");var subQ7=sQuery(id+"F0.wireOp",EDGE,"E25.3");Q4=makeQuery(id+"F8.boolean.opBoolean","INTERSECT",EDGE,{"derivedFrom":[makeQuery(id+"F5.boolean.opBoolean","SPLIT",FACE,{"disambiguationData":[TD([makeQuery(id+"F2.opExtrude","SWEPT_FACE",FACE,{"disambiguationData":[OSD([subQ5])]})])],"derivedFrom":makeQuery(id+"F3.boolean.opBoolean","COPY",FACE,{"derivedFrom":makeQuery(id+"F3.opExtrude","CAP_FACE",FACE,{"disambiguationData":[OSD([subQ5,subQ1,subQ6,subQ7,subQ4,subQ3,subQ2,subQ0])],"isStart":false})})}),makeQuery(id+"F8.opExtrude","SWEPT_FACE",FACE,{"disambiguationData":[OSD([sQuery(id+"F7.wireOp",EDGE,"E67")])]})]});}
            var Q5;
            Q5=makeQuery(id+"F8.boolean.opBoolean","INTERSECT",EDGE,{"disambiguationData":[OD(0.0)],"derivedFrom":[makeQuery(id+"F5.opExtrude","SWEPT_FACE",FACE,{"disambiguationData":[OSD([sQuery(id+"F4.wireOp",EDGE,"E30")])]}),makeQuery(id+"F8.opExtrude","SWEPT_FACE",FACE,{"disambiguationData":[OSD([sQuery(id+"F7.wireOp",EDGE,"E67")])]})]});
            fillet(context, id + "F14", {"entities" : qUnion([Q0, Q1, Q2, Q3, Q4, Q5]), "radius" : 3 * mm, "tangentPropagation" : true, "allowEdgeOverflow" : false});
        }
        {
            var Q0;
            Q0=makeQuery(id+"F1.opExtrude","CAP_EDGE",EDGE,{"disambiguationData":[OSD([sQuery(id+"F0.wireOp",EDGE,"E1.bottom")])],"isStart":false});
            fillet(context, id + "F15", {"entities" : qUnion([Q0]), "radius" : 2 * mm, "tangentPropagation" : true, "allowEdgeOverflow" : false});
        }
        {
            var Q0;
            {var subQ0=sQuery(id+"F0.wireOp",EDGE,"E21.filletArc");var subQ1=sQuery(id+"F0.wireOp",EDGE,"E7");var subQ2=sQuery(id+"F0.wireOp",EDGE,"E6");var subQ3=sQuery(id+"F0.wireOp",EDGE,"E5");var subQ4=sQuery(id+"F0.wireOp",EDGE,"E4");var subQ5=sQuery(id+"F0.wireOp",EDGE,"E22.filletArc");var subQ6=sQuery(id+"F0.wireOp",EDGE,"E1.bottom");var subQ7=sQuery(id+"F0.wireOp",EDGE,"E1.right");var subQ8=sQuery(id+"F0.wireOp",EDGE,"E1.top");var subQ9=sQuery(id+"F0.wireOp",EDGE,"E1.left");var subQ10=sQuery(id+"F0.wireOp",EDGE,"E23.filletArc");var subQ11=sQuery(id+"F0.wireOp",EDGE,"E24.filletArc");Q0=makeQuery(id+"F2.boolean.opBoolean","SPLIT",FACE,{"disambiguationData":[TD([makeQuery(id+"F1.opExtrude","SWEPT_FACE",FACE,{"disambiguationData":[OSD([subQ6])]})])],"derivedFrom":makeQuery(id+"F1.opExtrude","CAP_FACE",FACE,{"disambiguationData":[OSD([subQ6,subQ8,subQ9,subQ7,subQ4,subQ3,subQ2,subQ1,subQ0,subQ5,subQ10,subQ11])],"isStart":true})});}
            var sketch = newSketch(context, id + "F16", { "sketchPlane" : qUnion([Q0])});
            skLineSegment(sketch, "E79", {"start": v(-33, 90) * mm, "end": v(-15, 108) * mm});
            skLineSegment(sketch, "E80", {"start": v(-15, 108) * mm, "end": v(-15, 120) * mm});
            skLineSegment(sketch, "E81", {"start": v(15, 108) * mm, "end": v(33, 90) * mm});
            skLineSegment(sketch, "E82", {"start": v(15, 108) * mm, "end": v(15, 120) * mm});
            skArc(sketch, "E83", {"start": v(15, 120) * mm, "mid": v(0, 135) * mm, "end": v(-15, 120) * mm});
            skPoint(sketch, "E84.start.orphan", {"position": v(0, 90) * mm});
            skLineSegment(sketch, "E85", {"start": v(0, 90) * mm, "end": v(0, 120) * mm, "construction": true});
            skCircle(sketch, "E86", {"center": v(0, 120) * mm, "radius": 6 * mm});
            skLineSegment(sketch, "E87", {"start": v(0, 120) * mm, "end": v(6, 120) * mm});
            skPoint(sketch, "E88.end.orphan", {"position": v(-80, 0) * mm});
            skPoint(sketch, "E89.end.orphan", {"position": v(80, 0) * mm});
            skLineSegment(sketch, "E90", {"start": v(-80, 0) * mm, "end": v(80, 0) * mm, "construction": true});
            skLineSegment(sketch, "E91.MirrorCS", {"start": v(-15, -108) * mm, "end": v(-15, -120) * mm});
            skLineSegment(sketch, "E92.MirrorCS", {"start": v(15, -108) * mm, "end": v(33, -90) * mm});
            skLineSegment(sketch, "E93.MirrorCS", {"start": v(15, -108) * mm, "end": v(15, -120) * mm});
            skArc(sketch, "E94.MirrorCS", {"start": v(15, -120) * mm, "mid": v(0, -135) * mm, "end": v(-15, -120) * mm});
            skLineSegment(sketch, "E95.MirrorCS", {"start": v(-33, -90) * mm, "end": v(-15, -108) * mm});
            skCircle(sketch, "E96.MirrorC", {"center": v(0, -120) * mm, "radius": 6 * mm});
            skLineSegment(sketch, "E97.MirrorCS", {"start": v(0, -90) * mm, "end": v(0, -120) * mm, "construction": true});
            skSolve(sketch);
        }
        {
            var Q0;
            {var subQ1=sQuery(id+"F16.wireOp",EDGE,"E79");Q0=makeQuery(id+"F16.imprint","IMPRINT",FACE,{"disambiguationData":[TD([[makeQuery(id+"F16.imprint","IMPRINT",EDGE,{"derivedFrom":subQ1}),-1.0]])]});}
            var Q1;
            Q1=makeQuery(id+"F16.imprint","IMPRINT",FACE,{"disambiguationData":[TD([[makeQuery(id+"F16.imprint","IMPRINT",EDGE,{"derivedFrom":makeQuery(id+"F1.opExtrude","CAP_EDGE",EDGE,{"disambiguationData":[OSD([sQuery(id+"F0.wireOp",EDGE,"E1.left")])],"isStart":true})}),-1.0]])]});
            var Q2;
            Q2=makeQuery(id+"F16.imprint","IMPRINT",FACE,{"disambiguationData":[TD([[makeQuery(id+"F16.imprint","IMPRINT",EDGE,{"derivedFrom":sQuery(id+"F16.wireOp",EDGE,"E91.MirrorCS")}),1.0]])]});
            var Q3;
            Q3=makeQuery(id+"F2.opExtrude","CAP_FACE",FACE,{"disambiguationData":[OSD([sQuery(id+"F0.wireOp",EDGE,"E12"),sQuery(id+"F0.wireOp",EDGE,"E13"),sQuery(id+"F0.wireOp",EDGE,"E14"),sQuery(id+"F0.wireOp",EDGE,"E15"),sQuery(id+"F0.wireOp",EDGE,"E17.filletArc"),sQuery(id+"F0.wireOp",EDGE,"E18.filletArc"),sQuery(id+"F0.wireOp",EDGE,"E19.filletArc"),sQuery(id+"F0.wireOp",EDGE,"E20.filletArc"),sQuery(id+"F0.wireOp",EDGE,"E25.0"),sQuery(id+"F0.wireOp",EDGE,"E25.1"),sQuery(id+"F0.wireOp",EDGE,"E25.2"),sQuery(id+"F0.wireOp",EDGE,"E25.3"),sQuery(id+"F0.wireOp",EDGE,"E25.4"),sQuery(id+"F0.wireOp",EDGE,"E25.5"),sQuery(id+"F0.wireOp",EDGE,"E25.6"),sQuery(id+"F0.wireOp",EDGE,"E25.7")])],"isStart":false});
            extrude(context, id + "F17", {"entities" : qUnion([Q0, Q1, Q2]), "endBound" : BoundingType.UP_TO_SURFACE, "depth" : 25 * mm, "endBoundEntityFace" : qUnion([Q3]), "offsetDistance" : 25 * mm});
        }
    });
